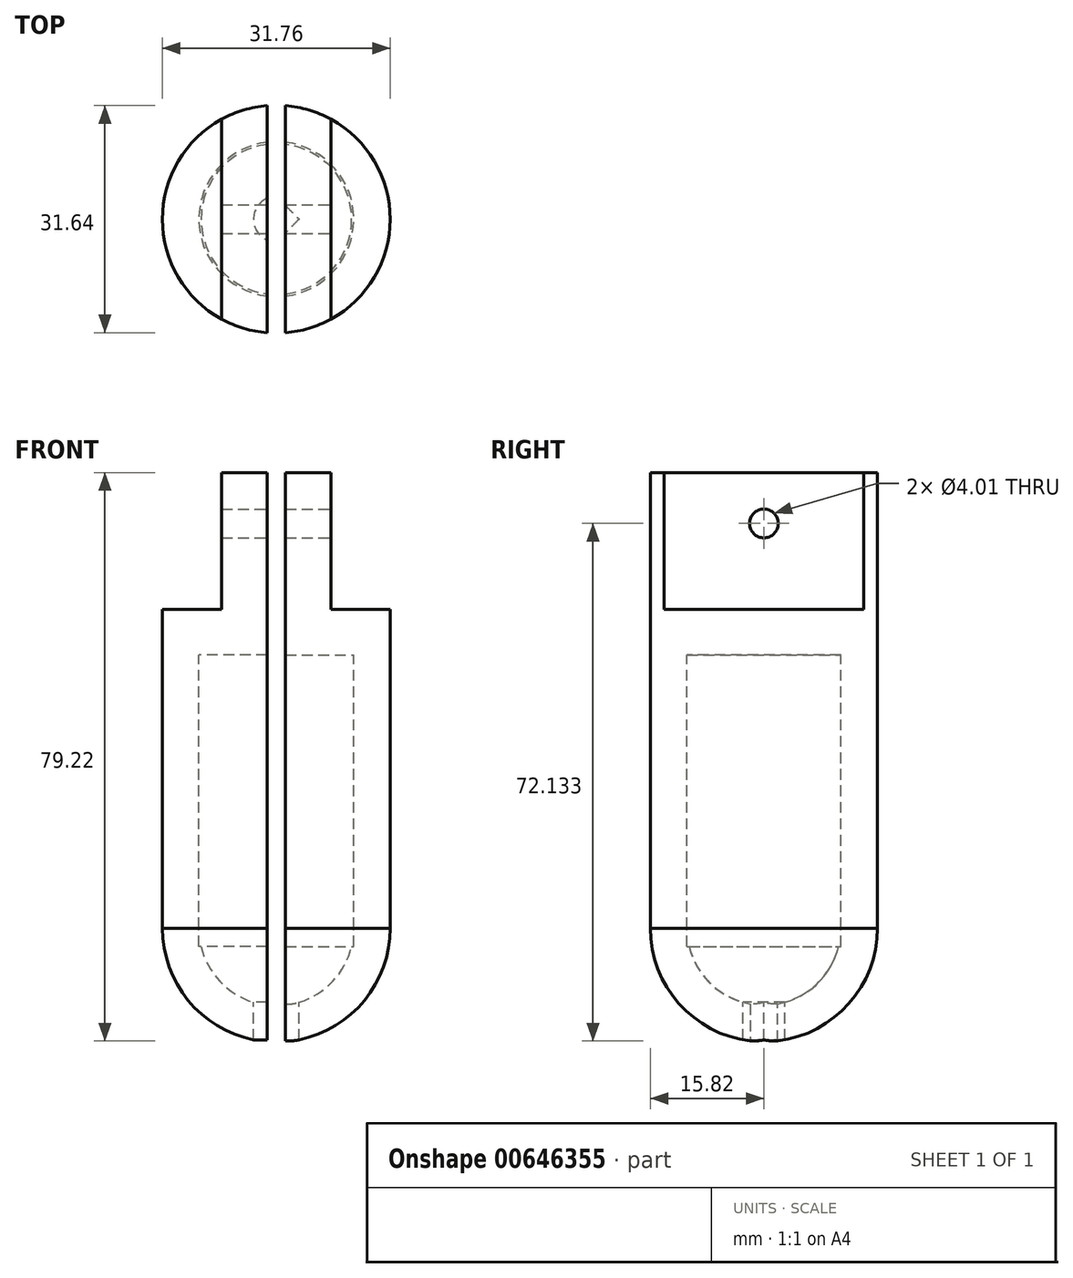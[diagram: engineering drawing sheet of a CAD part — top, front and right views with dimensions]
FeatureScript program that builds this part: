
annotation { "Feature Type Name" : "Feature", "Feature Type Description" : "" }
export const myFeature = defineFeature(function(context is Context, id is Id, definition is map)
    precondition{}
    {
        {
            var Q0;
            Q0=qCreatedBy(makeId("Top.planeOp"),FACE);
            var sketch = newSketch(context, id + "F0", { "sketchPlane" : qUnion([Q0])});
            skCircle(sketch, "E0", {"center": v(0, 0) * mm, "radius": 15.88 * mm});
            skSolve(sketch);
        }
        {
            var Q0;
            Q0 = qSketchRegion(id + "F0", true);
            extrude(context, id + "F1", {"entities" : qUnion([Q0]), "depth" : 38.1 * mm, "offsetDistance" : 25.4 * mm});
        }
        {
            var Q0;
            Q0=qCreatedBy(makeId("Front.planeOp"),FACE);
            var sketch = newSketch(context, id + "F2", { "sketchPlane" : qUnion([Q0])});
            skLineSegment(sketch, "E1", {"start": v(0, 0) * mm, "end": v(0, 16.58) * mm, "construction": true});
            skArc(sketch, "E2", {"start": v(0, -15.88) * mm, "mid": v(11.23, -11.23) * mm, "end": v(15.88, 0) * mm});
            skLineSegment(sketch, "E3", {"start": v(0, 0) * mm, "end": v(0, -15.88) * mm});
            skLineSegment(sketch, "E4", {"start": v(0, 0) * mm, "end": v(15.88, 0) * mm});
            skSolve(sketch);
        }
        {
            var Q0;
            Q0 = qSketchRegion(id + "F2", true);
            var Q1;
            Q1=sQuery(id+"F2.wireOp",EDGE,"E1");
            revolve(context, id + "F3", {"entities" : qUnion([Q0]), "axis" : qUnion([Q1]), "revolveType" : RevolveType.FULL});
        }
        {
            var Q0;
            Q0=makeQuery(id+"F3.opRevolve","SWEPT_FACE",FACE,{"disambiguationData":[OSD([sQuery(id+"F2.wireOp",EDGE,"E4")])]});
            shell(context, id + "F4", {"entities" : qUnion([Q0]), "thickness" : 5.08 * mm});
        }
        {
            var Q0;
            Q0=qCreatedBy(makeId("Top.planeOp"),FACE);
            var sketch = newSketch(context, id + "F5", { "sketchPlane" : qUnion([Q0])});
            skArc(sketch, "E5", {"start": v(0, 3.18) * mm, "mid": v(-3.18, 0) * mm, "end": v(0, -3.18) * mm});
            skLineSegment(sketch, "E6", {"start": v(0, 3.18) * mm, "end": v(0, -3.18) * mm});
            skSolve(sketch);
        }
        {
            var Q0;
            Q0 = qSketchRegion(id + "F5", true);
            extrude(context, id + "F6", {"entities" : qUnion([Q0]), "operationType" : NewBodyOperationType.REMOVE, "oppositeDirection" : true, "depth" : 25.4 * mm, "offsetDistance" : 25.4 * mm});
        }
        {
            var Q0;
            Q0=makeQuery(id+"F1.opExtrude","CAP_FACE",FACE,{"disambiguationData":[OSD([sQuery(id+"F0.wireOp",EDGE,"E0")])],"isStart":false});
            var sketch = newSketch(context, id + "F7", { "sketchPlane" : qUnion([Q0])});
            skCircle(sketch, "E7", {"center": v(0, 0) * mm, "radius": 10.8 * mm});
            skSolve(sketch);
        }
        {
            var Q0;
            Q0 = qSketchRegion(id + "F7", true);
            extrude(context, id + "F8", {"entities" : qUnion([Q0]), "operationType" : NewBodyOperationType.REMOVE, "oppositeDirection" : true, "depth" : 40.64 * mm, "offsetDistance" : 25.4 * mm});
        }
        {
            var Q0;
            Q0=qCreatedBy(makeId("Top.planeOp"),FACE);
            var sketch = newSketch(context, id + "F9", { "sketchPlane" : qUnion([Q0])});
            skLineSegment(sketch, "E8", {"start": v(0, 0) * mm, "end": v(0, 3.18) * mm});
            skLineSegment(sketch, "E9", {"start": v(0, 3.18) * mm, "end": v(3.18, 0) * mm});
            skLineSegment(sketch, "E10", {"start": v(3.17, 0) * mm, "end": v(0, -3.17) * mm});
            skLineSegment(sketch, "E11", {"start": v(0, -3.18) * mm, "end": v(0, 0) * mm});
            skSolve(sketch);
        }
        {
            var Q0;
            Q0 = qSketchRegion(id + "F9", true);
            extrude(context, id + "F10", {"entities" : qUnion([Q0]), "operationType" : NewBodyOperationType.REMOVE, "oppositeDirection" : true, "depth" : 25.4 * mm, "offsetDistance" : 25.4 * mm});
        }
        {
            var Q0;
            Q0=qCreatedBy(makeId("Front.planeOp"),FACE);
            var sketch = newSketch(context, id + "F11", { "sketchPlane" : qUnion([Q0])});
            skLineSegment(sketch, "E12.0", {"start": v(-1.27, 37.98) * mm, "end": v(-1.27, -17) * mm});
            skLineSegment(sketch, "E13.0", {"start": v(1.27, 37.98) * mm, "end": v(1.27, -17) * mm});
            skLineSegment(sketch, "E14", {"start": v(-1.27, 37.98) * mm, "end": v(-1.27, 38.56) * mm});
            skLineSegment(sketch, "E15", {"start": v(-1.27, 38.56) * mm, "end": v(1.27, 38.56) * mm});
            skLineSegment(sketch, "E16", {"start": v(1.27, 38.56) * mm, "end": v(1.27, 37.98) * mm});
            skLineSegment(sketch, "E17", {"start": v(-1.27, -17) * mm, "end": v(1.27, -17) * mm});
            skSolve(sketch);
        }
        {
            var Q0;
            Q0 = qSketchRegion(id + "F11", true);
            extrude(context, id + "F12", {"entities" : qUnion([Q0]), "operationType" : NewBodyOperationType.REMOVE, "endBound" : BoundingType.SYMMETRIC, "depth" : 38.1 * mm, "offsetDistance" : 25.4 * mm});
        }
        {
            var Q0;
            {var subQ0=sQuery(id+"F0.wireOp",EDGE,"E0");Q0=makeQuery(id+"F12.boolean.opBoolean","SPLIT",FACE,{"disambiguationData":[TD([makeQuery(id+"F12.opExtrude","SWEPT_FACE",FACE,{"disambiguationData":[OSD([sQuery(id+"F11.wireOp",EDGE,"E12.0"),sQuery(id+"F11.wireOp",EDGE,"E14")])]})])],"derivedFrom":makeQuery(id+"F1.opExtrude","CAP_FACE",FACE,{"disambiguationData":[OSD([subQ0])],"isStart":false})});}
            var sketch = newSketch(context, id + "F13", { "sketchPlane" : qUnion([Q0])});
            skLineSegment(sketch, "E18", {"start": v(-1.27, 15.82) * mm, "end": v(-1.27, -15.82) * mm});
            skArc(sketch, "E19", {"start": v(-1.27, 15.82) * mm, "mid": v(-15.87, 0) * mm, "end": v(-1.27, -15.82) * mm});
            skArc(sketch, "E20.MirrorCS", {"start": v(1.27, 15.82) * mm, "mid": v(15.87, 0) * mm, "end": v(1.27, -15.82) * mm});
            skLineSegment(sketch, "E21.MirrorCS", {"start": v(1.27, 15.82) * mm, "end": v(1.27, -15.82) * mm});
            skSolve(sketch);
        }
        {
            var Q0;
            Q0 = qSketchRegion(id + "F13", true);
            extrude(context, id + "F14", {"entities" : qUnion([Q0]), "operationType" : NewBodyOperationType.ADD, "depth" : 6.35 * mm, "offsetDistance" : 25.4 * mm});
        }
        {
            var Q0;
            Q0=makeQuery(id+"F14.opExtrude","CAP_FACE",FACE,{"disambiguationData":[OSD([sQuery(id+"F13.wireOp",EDGE,"E18"),sQuery(id+"F13.wireOp",EDGE,"E19")])],"isStart":false});
            var sketch = newSketch(context, id + "F15", { "sketchPlane" : qUnion([Q0])});
            skLineSegment(sketch, "E22", {"start": v(-1.27, 15.82) * mm, "end": v(-1.27, -15.82) * mm});
            skArc(sketch, "E23", {"start": v(-1.27, 15.82) * mm, "mid": v(-4.55, 15.21) * mm, "end": v(-7.62, 13.93) * mm});
            skLineSegment(sketch, "E24", {"start": v(-7.62, -13.93) * mm, "end": v(-7.62, 13.93) * mm});
            skArc(sketch, "E25.trimOffspring", {"start": v(-7.62, -13.93) * mm, "mid": v(-4.55, -15.21) * mm, "end": v(-1.27, -15.82) * mm});
            skLineSegment(sketch, "E26.MirrorCS", {"start": v(1.27, 15.82) * mm, "end": v(1.27, -15.82) * mm});
            skArc(sketch, "E27.MirrorCS", {"start": v(1.27, 15.82) * mm, "mid": v(4.55, 15.21) * mm, "end": v(7.62, 13.93) * mm});
            skLineSegment(sketch, "E28.MirrorCS", {"start": v(7.62, -13.93) * mm, "end": v(7.62, 13.93) * mm});
            skArc(sketch, "E29.MirrorCS", {"start": v(7.62, -13.93) * mm, "mid": v(4.55, -15.21) * mm, "end": v(1.27, -15.82) * mm});
            skSolve(sketch);
        }
        {
            var Q0;
            Q0 = qSketchRegion(id + "F15", true);
            extrude(context, id + "F16", {"entities" : qUnion([Q0]), "operationType" : NewBodyOperationType.ADD, "depth" : 19.05 * mm, "offsetDistance" : 25.4 * mm});
        }
        {
            var Q0;
            Q0=qCreatedBy(makeId("Right.planeOp"),FACE);
            var sketch = newSketch(context, id + "F17", { "sketchPlane" : qUnion([Q0])});
            skCircle(sketch, "E30", {"center": v(0, 56.41) * mm, "radius": 2 * mm});
            skSolve(sketch);
        }
        {
            var Q0;
            Q0 = qSketchRegion(id + "F17", true);
            extrude(context, id + "F18", {"entities" : qUnion([Q0]), "operationType" : NewBodyOperationType.REMOVE, "endBound" : BoundingType.SYMMETRIC, "oppositeDirection" : true, "depth" : 25.4 * mm, "offsetDistance" : 25.4 * mm});
        }
    });
